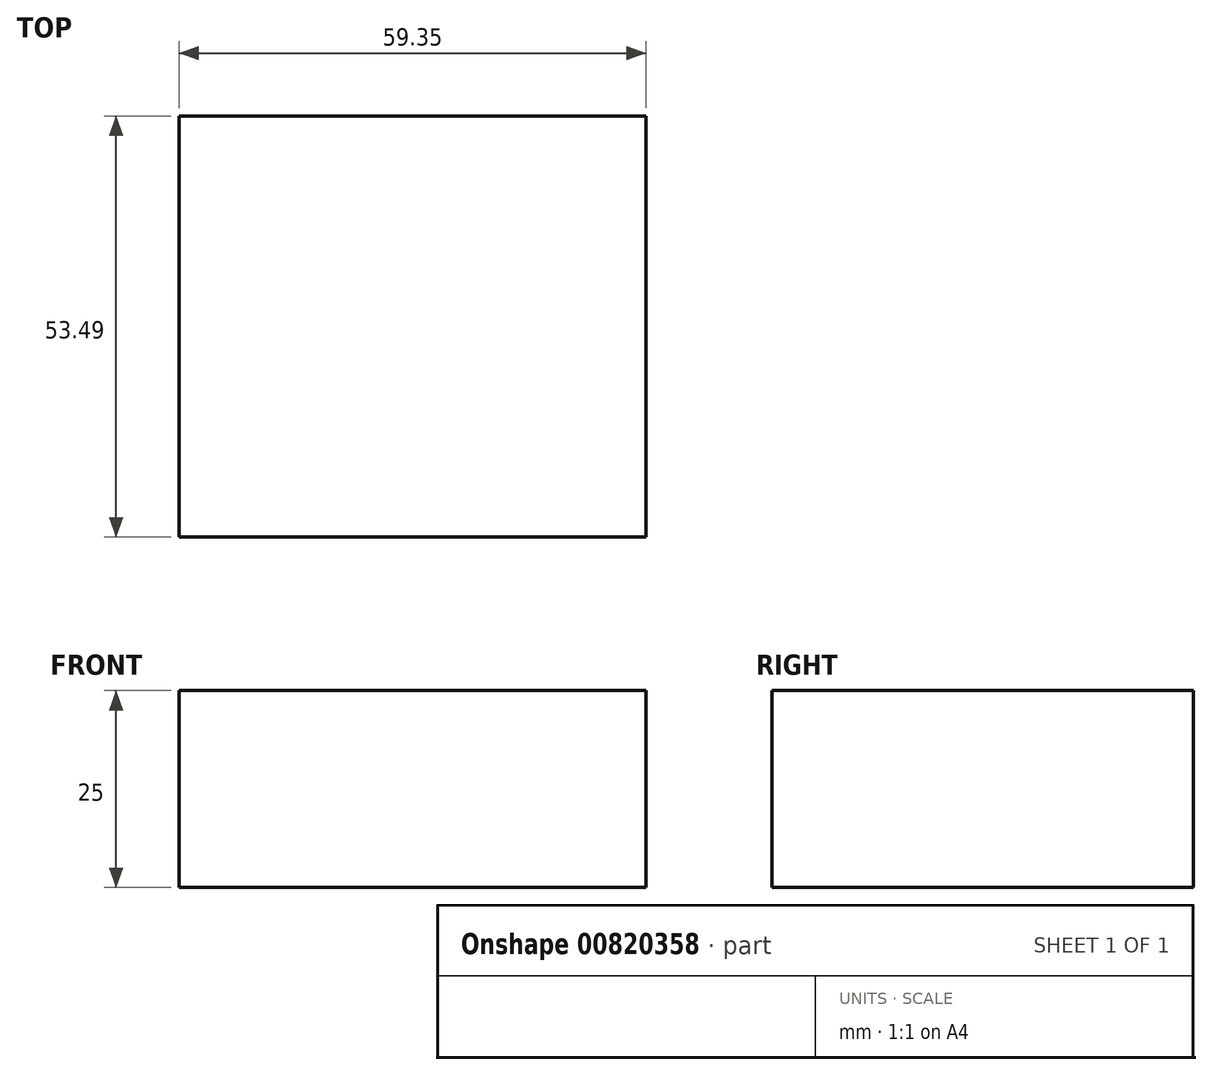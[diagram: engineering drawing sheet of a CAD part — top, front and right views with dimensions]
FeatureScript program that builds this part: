
annotation { "Feature Type Name" : "Feature", "Feature Type Description" : "" }
export const myFeature = defineFeature(function(context is Context, id is Id, definition is map)
    precondition{}
    {
        {
            var Q0;
            Q0=qCreatedBy(makeId("Top.planeOp"),FACE);
            var sketch = newSketch(context, id + "F0", { "sketchPlane" : qUnion([Q0])});
            skLineSegment(sketch, "E0.bottom", {"start": v(19.13, -26.47) * mm, "end": v(-40.22, -26.47) * mm});
            skLineSegment(sketch, "E0.top", {"start": v(19.13, 27.02) * mm, "end": v(-40.22, 27.02) * mm});
            skLineSegment(sketch, "E0.left", {"start": v(19.13, -26.47) * mm, "end": v(19.13, 27.02) * mm});
            skLineSegment(sketch, "E0.right", {"start": v(-40.22, -26.47) * mm, "end": v(-40.22, 27.02) * mm});
            skSolve(sketch);
        }
        {
            var Q0;
            Q0=makeQuery(id+"F0.imprint","IMPRINT",FACE,{"disambiguationData":[TD([[makeQuery(id+"F0.imprint","IMPRINT",EDGE,{"derivedFrom":sQuery(id+"F0.wireOp",EDGE,"E0.bottom")}),-1.0]])]});
            extrude(context, id + "F1", {"entities" : qUnion([Q0]), "depth" : 25 * mm, "offsetDistance" : 25 * mm});
        }
    });
